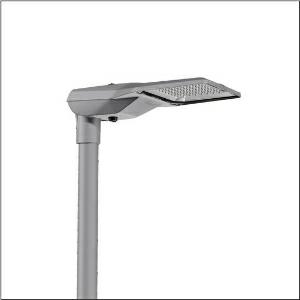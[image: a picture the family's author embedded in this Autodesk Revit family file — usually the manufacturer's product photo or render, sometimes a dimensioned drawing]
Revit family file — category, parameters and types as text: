
# Revit family: streetlight_sl_21_midi___pl52_5xe3h33t08mb_7712
name_source: partatom
category: Lighting Fixtures
units: mm (PartAtom-declared; Revit-internal decimal feet)

## family parameters
Cut with Voids When Loaded = No
Host = Face
Light Source = No
Part Type = Normal
Room Calculation Point = No
Round Connector Dimension = Use Diameter
Shared = No

## types (1)
- --- (1 x LED, 17960 lm, 136 W, 3000K)
    Apparent Load = 136 VA
    CIE Flux Codes = 27 59 98 100 100
    Color Rendering = 70
    Color Temperature = 3000K
    Default Elevation = 1800 mm
    Description = Streetlight SL 21 midi, mast luminaire, primary light control with lens, of PMMA, primary optical cover: cover, of toughened safety glass, transparent, light distribution: PL52, light emission: direct distribution, primary light characteristic: asymmetric, installation type: side-entry, post-top, LED, High Power LED, rated luminous flux: 17.960lm, luminous efficacy: 132lm/W, light colour: 730, colour temperature: 3000K, control gear: D4i, control: overheat protection, constant luminous flux control, time-dependent luminous flux control, flexible luminous flux parameterisation, pre-setting: logarithmic dimming characteristic, mains connection: 230..240V, AC, 50/60Hz, start of lifetime: 136W, end of service life: 142W, reduction: 61W, luminaire housing, of diecast aluminium, powder-coated, Siteco® metallic grey (DB 702S), corrosivity category C5 mid according to DIN EN ISO 12944, please order mast flange separately, inclination adjustable: 0°, 5°, 10°, 15°, sealing non-destructively replaceable, multi-level sealing system, length: 644mm, width: 335mm, height: 110mm, mast flange for spigot size: 42mm (side-entry): 5XC10008XM4, 60/48mm (side-entry/post-top): 5XC10108XM2, 76/60mm (side-entry/post-top): 5XC10108XM1, mounting height: 4..8m, Smart Interface below and above, protection rating (complete): IP66, insulation class (complete): insulation class II (safety insulation), certification: CE, ENEC, ENEC+, VDE, impact resistance: IK10, permissible operating ambient temperature for outdoor applications: -40..+50°C, standard-compliant lighting for roads and squares, packaging unit: 1 piece

Light Distribution: PL52
    Height = 111 mm
    Lamp = 1 x LED
    Lamp Light Flux = 17960 lm
    Lamp Power = 136 W
    Lamp count = 1
    Length = 644 mm
    Luminous efficacy = 132 lm/W
    Manufacturer = Siteco
    ModVariant = No
    Model = 5XE3H33T08MB
    Number of Poles = 1
    OnlyDefault = Yes
    Power Factor = 1
    Product Name = Streetlight SL 21 midi | PL52
    Product group = mast luminaire | pylon top
    ProductGroupID = 6100
    Protection Class = Protection class II
    Protection Degree = IP 66
    RLX_Detail_Level = 1
    RLX_Emergency_Light_Flux = 0 lm
    RLX_Emergency_Type = 0
    RLX_Emergency_Type_DB = No
    RlxData = <blob elided: 36641 chars, md5=c9f38cef>
    Socket = socket
    Standby Power = 0 W
    System Light Flux = 17960 lm
    System Power = 136 W
    Type Comments = factory setting: luminous flux: 100 % | dim-lin: 254 | 695 mA
    Type Image = l_1004304.jpg
    URL = http://relux.com
    VarID = @adj_211889
    Voltage = 0 V
    Weight = 0.00 kg
    Width = 336 mm

## geometry (parser evidence)
native form markers: Blend x4, Sweep x8
no freeform markers — native parametric forms only
